# Revit family: Drain_Trench_21_Inch_Wide_Reveal-Zurn-Z874-21
name_source: partatom
category: Plumbing Fixtures
units: mm (PartAtom-declared; Revit-internal decimal feet)

## family parameters
Always vertical = Yes
Cut with Voids When Loaded = No
Maintain Annotation Orientation = No
OmniClass Number = 23.70.50.21.24.14
OmniClass Title = Deck Waste Water Drains
Part Type = Normal
Room Calculation Point = No
Round Connector Dimension = Use Radius
Shared = No
Work Plane-Based = No

## types (1)
- Load Family Type Catalog
    Assembly Code = D2030300
    Bottom Outlet = No
    CW Connection = No
    CWFU = 1
    Connector Radius = 2 "
    Deep Invert = 12.08 "
    Default Elevation = 20 "
    Description = 21 [533] WIDE THROAT TRENCH DRAIN SYSTEM
    End outlet = Yes
    Flow = 4559 GPM
    Frame Material = Steel - Zurn - Carbon- Power coated Black
    Grate Material = Iron - Zurn - Cast - Ductile - Painted Black
    HW Connection = No
    HWFU = 1
    Main Material = Polymer - Zurn - HDPE - Grey
    Manufacturer = Zurn
    Manufacturer Brand = Zurn Water, LLC
    Model = Z874-21-1201P-HD
    Modified Date = 12/26/2025
    Outlet Size = 4 "
    Outlet offset = 3 "
    Pipe Size_ A Outer Radius = 2.25 "
    Pipe Size_A Inside Diameter = 4.026 "
    Pipe Size_A Nominal Diameter = 4 "
    Pipe Size_A Outer Diameter = 4.5 "
    Product Documentation Link = https://files.zurn.com
    Product Installation Sheet URL = https://files.zurn.com
    Product Page URL = https://www.zurn.com
    Product data url = https://www.bimobject.com
    Shallow Invert = 11.25 "
    Type Comments = Z874-21-1201P-80 x 21.25 x 10.082 with Heavy-Duty Frame
    URL = http://www.zurn.com
    Vent Connection = No
    WFU = 0
    Waste Connection = Yes

## geometry (parser evidence)
native form markers: Blend x4, Sweep x5
no freeform markers — native parametric forms only
